# Revit family: ef_eg-20_60ysd2_asd2_bsd2_btd2_dtc2_ftc-v_50Hz
name_source: partatom
category: 機械設備
units: mm (PartAtom-declared; Revit-internal decimal feet)

## family parameters
OmniClass タイトル = Industrial Ventilating Equipment
OmniClass 番号 = 23.75.35.21.17
パーツ タイプ = 標準
ロード時にボイドで切り取り = はい
丸型コネクタ寸法 = 直径を使用
作業面ベース = いいえ
共有 = いいえ
常に垂直 = はい
部屋計算ポイント = はい

## types (7) — shared parameters
IfcExportAs = IfcFanType
IfcExportType = TUBEAXIAL
MID風量 = 0.0 m³/h
MIN風量 = 0.0 m³/h
OmniClassCode = 23-33 31 19 11 17
URL = https://www.mitsubishielectric.co.jp
Uniclass2015Code = Pr_65_67_29_67
Uniclass2015Title = Propeller fans
Uniclass2015Version = Systems v1.9
ファンの種類 = 軸流羽根
フレームの厚さ = 10  [stored 0.0328084 ft]
仕様書バージョン = Version1.0
企業コード = 108420
分類コード = 50052503100110
周波数 = 50 Hz
呼称 = 有圧扇
法定耐用年数 = 15
製品リリース年月 = 2022年6月1日
製品出荷対象 = 国内
製造元 = 三菱電機株式会社
設置方法 = 壁付
説明 = 産業用有圧換気扇 防爆形
負荷分類 = 3_ファン類
運転質量 = 0.00 kg

## per-type parameters (varying)
| type | Depth | Height | MAX風量 | Width | オリフィス_Depth | オリフィス径 | モーター径 | レグ_Depth | レグ_Height | レグ_Width | 価格 | 極 | 極数 | 消費電力 | 相 | 羽根径 | 製品質量 | 質量 | 電動機出力 | 電圧 |
| EF-20YSD2-V | 295  [stored 0.967848 ft] | 320  [stored 1.04987 ft] | 670.0 m³/h | 320  [stored 1.04987 ft] | 50  [stored 0.164042 ft] | 245  [stored 0.803806 ft] | 108  [stored 0.354331 ft] | 167  [stored 0.5479 ft] | 260  [stored 0.853018 ft] | 260  [stored 0.853018 ft] | 162000 $ | 4 | 2 | 27 W | 1 | ∅200 | 6.50 kg | 7.80 kg | 15 W | 100 V |
| EF-25ASD2-V | 300 | 370 | 1170.0 m³/h | 370 | 60 | 310 | 108  [stored 0.354331 ft] | 166 | 300 | 300 | 171000 $ | 4 | 2 | 35 W | 1 | ∅250 | 6.90 kg | 8.28 kg | 25 W | 100 V |
| EF-30BSD2-V | 310 | 420 | 1700.0 m³/h | 420 | 60 | 365 | 108  [stored 0.354331 ft] | 182 | 347 | 347 | 222000 $ | 4 | 2 | 61 W | 1 | ∅300 | 7.50 kg | 9.00 kg | 50 W | 100 V |
| EF-30BTD2-V | 310 | 420 | 1700.0 m³/h | 420 | 60 | 365 | 108  [stored 0.354331 ft] | 182 | 347 | 347 | 222000 $ | 4 | 3 | 47 W | 3 | ∅300 | 7.50 kg | 9.00 kg | 50 W | 200 V |
| EF-40DTC2-V | 345 | 520 | 3860.0 m³/h | 520 | 80 | 490 | 140 | 215 | 396 | 396 | 264000 $ | 4 | 3 | 122 W | 3 | ∅400 | 21.60 kg | 25.92 kg | 200 W | 200 V |
| EG-50DTC2-V | 349 | 620 | 4960.0 m³/h | 620 | 95 | 605 | 140 | 217 | 500 | 500 | 329000 $ | 6 | 3 | 142 W | 3 | ∅500 | 26.80 kg | 32.16 kg | 200 W | 200 V |
| EG-60FTC-V | 419 | 710 | 10100.0 m³/h | 710 | 100  [stored 0.328084 ft] | 705 | 210 | 304 | 566 | 566 | 441000 $ | 6 | 3 | 475 W | 3 | ∅600 | 48.80 kg | 58.56 kg | 750 W | 200 V |

note: column(s) folded — value = type name in every type: モデル

note: [stored X ft] marks values corroborated as IEEE doubles in the binary element streams (Revit-internal decimal feet)
